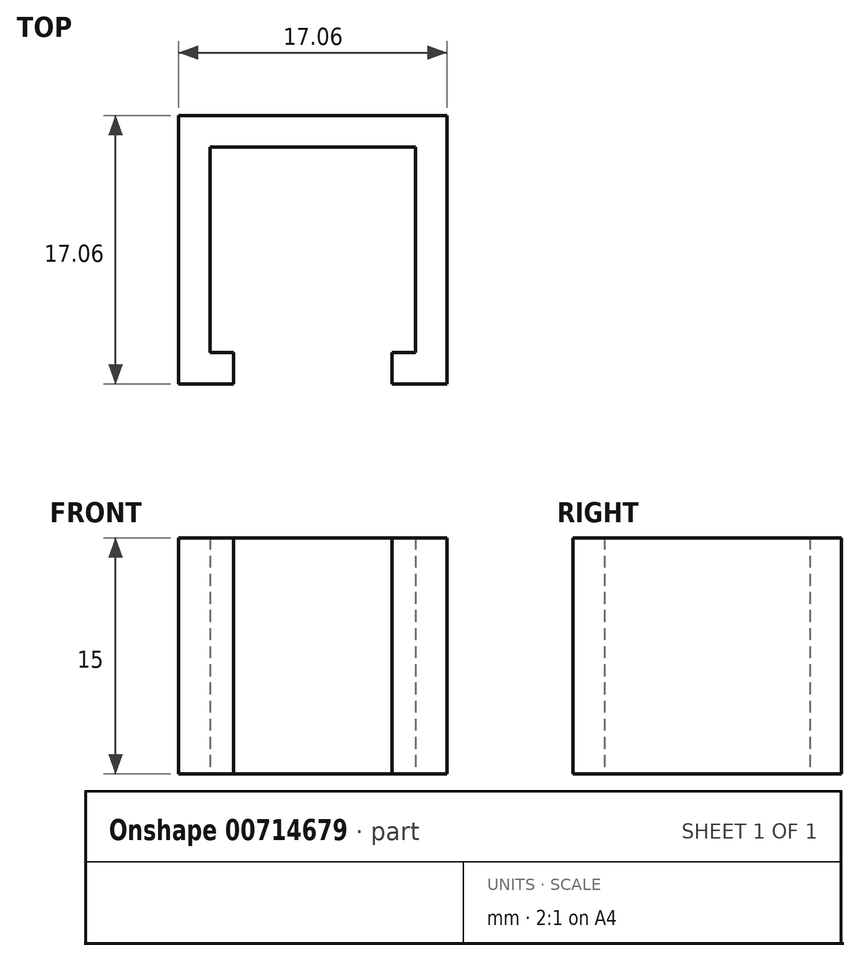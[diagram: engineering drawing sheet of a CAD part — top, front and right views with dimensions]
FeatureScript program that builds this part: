
annotation { "Feature Type Name" : "Feature", "Feature Type Description" : "" }
export const myFeature = defineFeature(function(context is Context, id is Id, definition is map)
    precondition{}
    {
        {
            var Q0;
            Q0=qCreatedBy(makeId("Top.planeOp"),FACE);
            var sketch = newSketch(context, id + "F0", { "sketchPlane" : qUnion([Q0])});
            skLineSegment(sketch, "E0.bottom", {"start": v(-6.52, 6.52) * mm, "end": v(6.53, 6.52) * mm});
            skLineSegment(sketch, "E0.top", {"start": v(-6.53, -6.53) * mm, "end": v(6.52, -6.53) * mm});
            skLineSegment(sketch, "E0.left", {"start": v(-6.52, 6.53) * mm, "end": v(-6.53, -6.52) * mm});
            skLineSegment(sketch, "E0.right", {"start": v(6.53, 6.53) * mm, "end": v(6.52, -6.53) * mm});
            skPoint(sketch, "E0.middle", {"position": v(0, 0) * mm});
            skLineSegment(sketch, "E1", {"start": v(-5.03, -6.53) * mm, "end": v(-5.03, -8.53) * mm});
            skLineSegment(sketch, "E2", {"start": v(-5.03, -8.53) * mm, "end": v(-8.53, -8.53) * mm});
            skLineSegment(sketch, "E3", {"start": v(-8.53, -8.53) * mm, "end": v(-8.53, 8.53) * mm});
            skLineSegment(sketch, "E4", {"start": v(-8.53, 8.53) * mm, "end": v(8.53, 8.53) * mm});
            skLineSegment(sketch, "E5", {"start": v(8.53, 8.53) * mm, "end": v(8.52, -8.53) * mm});
            skLineSegment(sketch, "E6", {"start": v(8.52, -8.53) * mm, "end": v(5.02, -8.53) * mm});
            skLineSegment(sketch, "E7", {"start": v(5.02, -8.53) * mm, "end": v(5.02, -6.53) * mm});
            skSolve(sketch);
        }
        {
            var Q0;
            Q0=makeQuery(id+"F0.imprint","IMPRINT",FACE,{"disambiguationData":[TD([[makeQuery(id+"F0.imprint","IMPRINT",EDGE,{"derivedFrom":sQuery(id+"F0.wireOp",EDGE,"E0.bottom")}),1.0]])]});
            extrude(context, id + "F1", {"entities" : qUnion([Q0]), "endBound" : BoundingType.SYMMETRIC, "depth" : 15 * mm, "offsetDistance" : 25 * mm});
        }
    });
